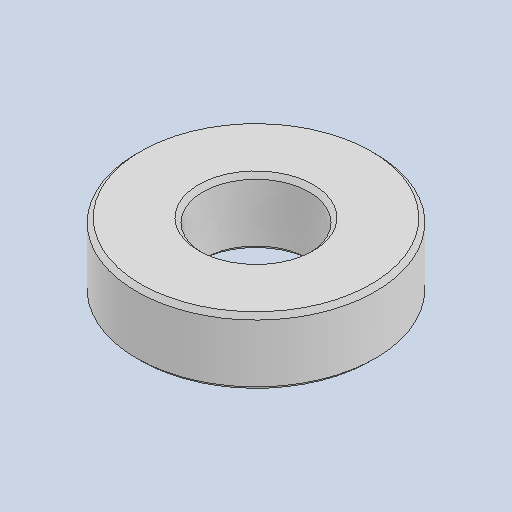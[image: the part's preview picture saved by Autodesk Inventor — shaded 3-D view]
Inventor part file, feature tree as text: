
AUTODESK INVENTOR PART (.ipt)
format: ipt  version: 2022.3 (Build 263350000, 350)  size: 96,768 bytes
history: native  units: in
note: dims shown in document units (in); Inventor stores cm internally (conversion verified against a paired STEP export)
features: chamfer x1
ambient origin geometry x8: Origin, YZ Plane, XZ Plane, XY Plane, X Axis, Y Axis, Z Axis, Center Point
bodies: Solid1 (feature_tree)
feature tree (1):
  chamfer  "Chamfer1"  [1 undecoded]
note: 1 required parameter value undecoded (feature->parameter linkage not recoverable at this tier; creation-order binding heuristic only, values carry confidence <= 0.55)
